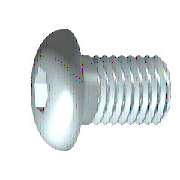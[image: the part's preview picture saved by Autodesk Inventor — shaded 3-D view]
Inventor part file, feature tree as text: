
AUTODESK INVENTOR PART (.ipt)
format: ipt  version: 2013 (Build 170138000, 138)  size: 188,416 bytes
history: native  units: mm (DEFAULTED — no unit token found)
features: sketch x2, extrude x1, plane x1, fillet x1
ambient origin geometry x7: Origin, YZ Plane, XY Plane, X Axis, Y Axis, Z Axis, Center Point
bodies: Solid1 (feature_tree), Body (feature_tree)
feature tree (5):
  extrude  "Slot"  Depth=1.59014mm
  plane  "Work Plane1"
  fillet  "Fillet2"  Radius=2.2098mm
  sketch  "Sketch1"  dims[d1=20.63476mm d2=1.59014mm d3=2.2098mm]
  sketch  "Sketch2"  dims[d4=1.3208mm d5=60.0deg d6=4.1656mm d7=4.1656mm d8=2.756963mm d9=7.9248mm d10=90.0deg d11=10.0mm d12=0.0mm d13=20.63476mm d14=0.0mm d15=0.486918mm d16=0.486918mm d17=1.9558mm d19=0.0mm d26=22.225mm d27=45.0deg d28=0.0mm d29=0.0mm d30=0.1mm]
